# Revit family: TowelRail_SurfaceMount_Abey_Vela_Double
name_source: partatom
category: Specialty Equipment
units: mm (PartAtom-declared; Revit-internal decimal feet)

## family parameters
Always vertical = Yes
Cut with Voids When Loaded = No
OmniClass Number = 23.31.25.25
OmniClass Title = Towel Bars
Part Type = Normal
Room Calculation Point = No
Round Connector Dimension = Use Diameter
Shared = No
Work Plane-Based = No

## types (5) — shared parameters
Assembly Code = C1030210
IfcExportAs = IfcFurniture
IfcExportType = NOTDEFINED
Manufacturer = Abey
ManufacturerOverallDepth = 113 mm  [stored 0.370735 ft]
ManufacturerOverallHeight = 25 mm  [stored 0.082021 ft]
ManufacturerOverallWidth = 760 mm  [stored 2.49344 ft]
ManufacturerURLProductSpecific = https://www.abey.com.au
ModifiedIssue = 20241025 $
URL = https://www.abey.com.au
Uniclass2015Code = Pr_40_20_76_90
Uniclass2015Title = Towel rails
Uniclass2015Version = Products v1.33
zero-valued in all types: Default Elevation

## per-type parameters (varying)
| type | Description | ManufacturerSpecCode | Material | Model | Type Comments |
| Chrome (VDTR) | Vela Double Towel Rail Chrome | VDTR | Metal_Abey_Chrome | VDTR | Chrome |
| Black (VDTR-B) | Vela Double Towel Rail Black | VDTR-B | Metal_Abey_Black | VDTR-B | Black |
| Brushed Brass (VDTR-BB) | Vela Double Towel Rail Brushed Brass | VDTR-BB | Metal_Abey_Brass | VDTR-BB | Brushed Brass |
| Gun Metal (VDTR-GM) | Vela Double Towel Rail Gun Metal | VDTR-GM | Metal_Abey_GunMetal | VDTR-GM | Gun Metal |
| Brushed Nickel (VDTR-BN) | Vela Double Towel Rail Brushed Nickel | VDTR-BN | Metal_Abey_BrushedNickel | VDTR-BN | Brushed Nickel |

note: [stored X ft] marks values corroborated as IEEE doubles in the binary element streams (Revit-internal decimal feet)

## geometry (parser evidence)
native form markers: Sweep x2
no freeform markers — native parametric forms only
